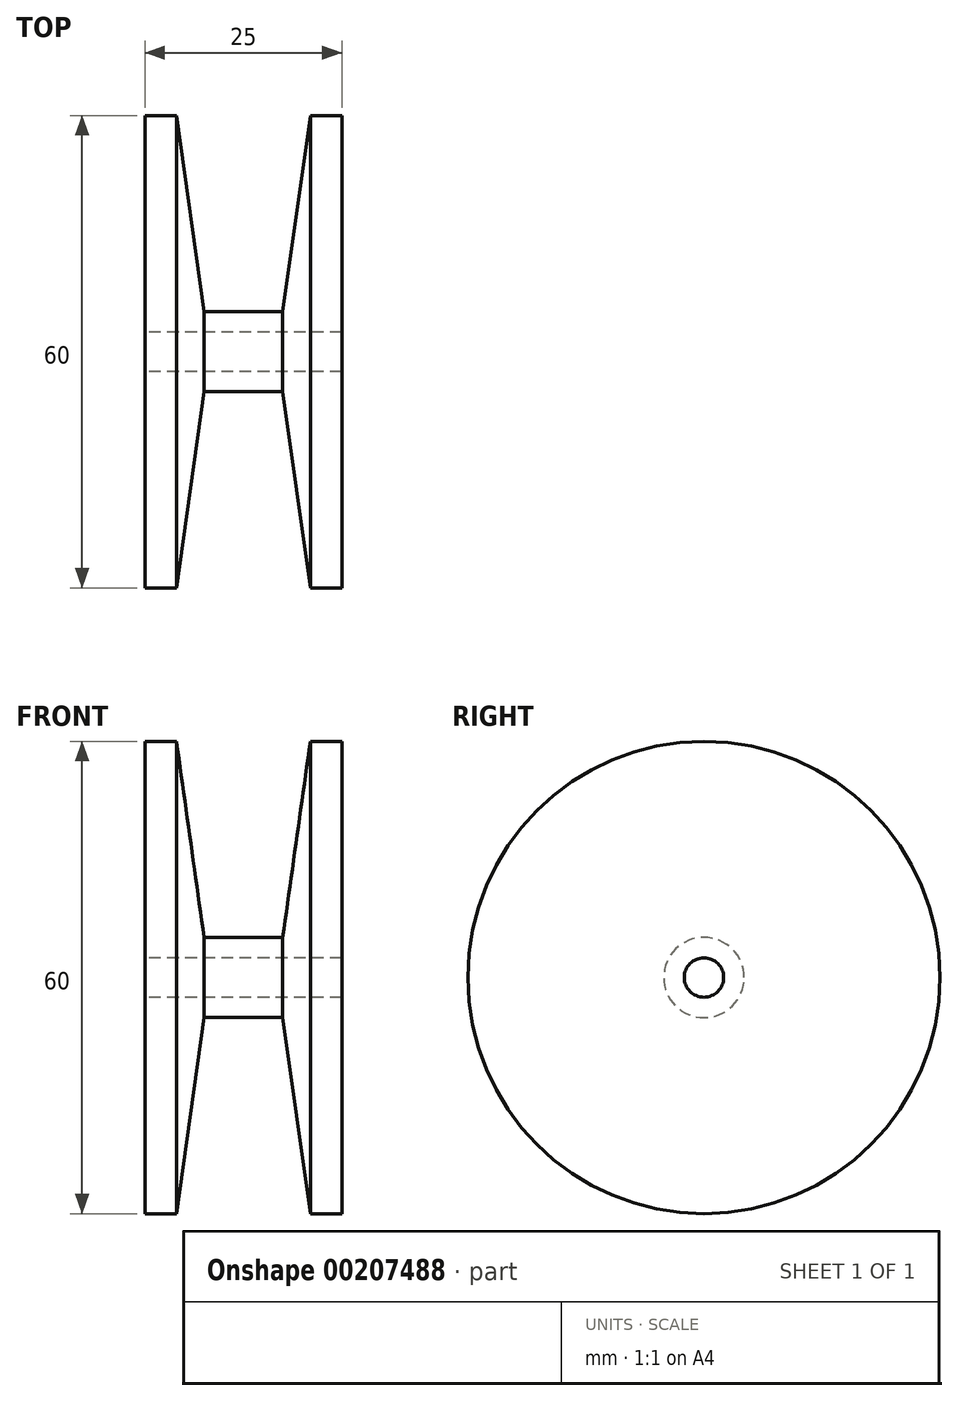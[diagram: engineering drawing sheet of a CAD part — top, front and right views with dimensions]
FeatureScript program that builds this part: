
annotation { "Feature Type Name" : "Feature", "Feature Type Description" : "" }
export const myFeature = defineFeature(function(context is Context, id is Id, definition is map)
    precondition{}
    {
        {
            var Q0;
            Q0=qCreatedBy(makeId("Front.planeOp"),FACE);
            var sketch = newSketch(context, id + "F0", { "sketchPlane" : qUnion([Q0])});
            skLineSegment(sketch, "E0", {"start": v(0, 0) * mm, "end": v(25, 0) * mm});
            skLineSegment(sketch, "E1", {"start": v(25, 0) * mm, "end": v(25, 30) * mm});
            skLineSegment(sketch, "E2", {"start": v(25, 30) * mm, "end": v(21, 30) * mm});
            skLineSegment(sketch, "E3", {"start": v(21, 30) * mm, "end": v(17.5, 5.1) * mm});
            skLineSegment(sketch, "E4", {"start": v(17.5, 5.1) * mm, "end": v(7.5, 5.1) * mm});
            skLineSegment(sketch, "E5", {"start": v(7.5, 5.1) * mm, "end": v(4, 30) * mm});
            skLineSegment(sketch, "E6", {"start": v(4, 30) * mm, "end": v(0, 30) * mm});
            skLineSegment(sketch, "E7", {"start": v(0, 30) * mm, "end": v(0, 0) * mm});
            skPoint(sketch, "E8", {"position": v(12.5, 0) * mm});
            skPoint(sketch, "E9", {"position": v(12.5, 5.1) * mm});
            skSolve(sketch);
        }
        {
            var Q0;
            Q0=makeQuery(id+"F0.imprint","IMPRINT",FACE,{"disambiguationData":[TD([[makeQuery(id+"F0.imprint","IMPRINT",EDGE,{"derivedFrom":sQuery(id+"F0.wireOp",EDGE,"E0")}),1.0]])]});
            var Q1;
            Q1=sQuery(id+"F0.wireOp",EDGE,"E0");
            revolve(context, id + "F1", {"entities" : qUnion([Q0]), "axis" : qUnion([Q1]), "revolveType" : RevolveType.FULL});
        }
        {
            var Q0;
            Q0=makeQuery(id+"F1.opRevolve","SWEPT_FACE",FACE,{"disambiguationData":[OSD([sQuery(id+"F0.wireOp",EDGE,"E7")])]});
            var sketch = newSketch(context, id + "F2", { "sketchPlane" : qUnion([Q0])});
            skCircle(sketch, "E10.0.0", {"center": v(0, 0) * mm, "radius": 30 * mm});
            skCircle(sketch, "E11", {"center": v(0, 0) * mm, "radius": 2.5 * mm});
            skSolve(sketch);
        }
        {
            var Q0;
            Q0=makeQuery(id+"F2.imprint","IMPRINT",FACE,{"disambiguationData":[TD([[makeQuery(id+"F2.imprint","IMPRINT",EDGE,{"derivedFrom":sQuery(id+"F2.wireOp",EDGE,"E11")}),1.0]])]});
            extrude(context, id + "F3", {"entities" : qUnion([Q0]), "operationType" : NewBodyOperationType.REMOVE, "endBound" : BoundingType.THROUGH_ALL, "oppositeDirection" : true, "depth" : 25 * mm});
        }
    });
